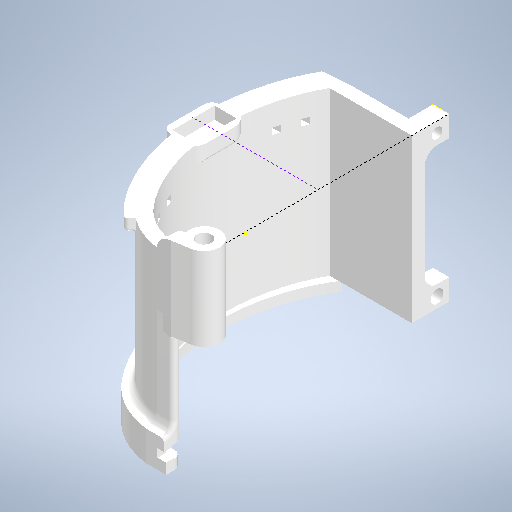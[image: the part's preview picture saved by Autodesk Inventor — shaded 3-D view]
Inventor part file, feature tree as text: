
AUTODESK INVENTOR PART (.ipt)
format: ipt  version: 2025.2 (Build 292293000, 293)  size: 586,240 bytes
history: native  units: in
note: dims shown in document units (in); Inventor stores cm internally (conversion verified against a paired STEP export)
features: sketch x6, fillet x6, extrude x2
ambient origin geometry x8: Origin, YZ Plane, XZ Plane, XY Plane, X Axis, Y Axis, Z Axis, Center Point
bodies: Solid1 (feature_tree), Body1 (feature_tree)
feature tree (14):
  sketch  "Sketch1"  dims[d5=0.1693in d6=0.2441in]
  sketch  "Sketch2"  dims[d7=0.0787in d8=0.0in d9=0.1063in d10=0.2047in d11=0.0591in d12=0.0in d13=0.0787in d14=0.0394in d15=0.0394in d16=0.0197in]
  sketch  "Sketch4"  dims[d17=0.0197in]
  sketch  "Sketch5"  dims[d18=0.0787in]
  extrude  "Extrusion1"  Depth=0.2441in
  extrude  "Extrusion2"  Depth=0.1063in
  fillet  "Fillet1"  Radius=0.2047in
  fillet  "Fillet2"  Radius=0.0591in
  fillet  "Fillet3"  Radius=0.0787in
  fillet  "Fillet4"  Radius=0.0394in
  fillet  "Fillet5"  Radius=0.0394in
  fillet  "Fillet6"  Radius=0.0197in
  sketch  "Sketch6"
  sketch  "Sketch7"
